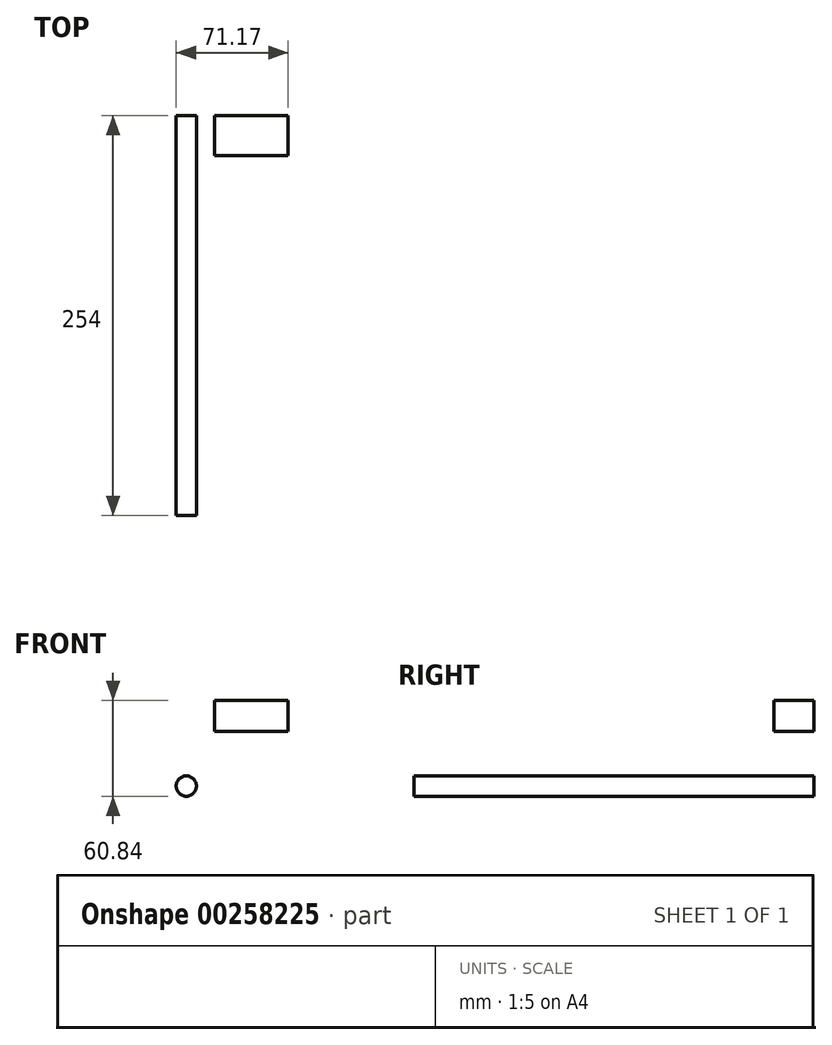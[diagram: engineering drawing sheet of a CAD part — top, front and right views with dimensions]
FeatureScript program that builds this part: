
annotation { "Feature Type Name" : "Feature", "Feature Type Description" : "" }
export const myFeature = defineFeature(function(context is Context, id is Id, definition is map)
    precondition{}
    {
        {
            var Q0;
            Q0=qCreatedBy(makeId("Front.planeOp"),FACE);
            var sketch = newSketch(context, id + "F0", { "sketchPlane" : qUnion([Q0])});
            skCircle(sketch, "E0", {"center": v(0, 0) * mm, "radius": 6.46 * mm});
            skLineSegment(sketch, "E1.bottom", {"start": v(17.88, 54.38) * mm, "end": v(64.7, 54.38) * mm});
            skLineSegment(sketch, "E1.top", {"start": v(17.88, 34.84) * mm, "end": v(64.7, 34.84) * mm});
            skLineSegment(sketch, "E1.left", {"start": v(17.88, 54.38) * mm, "end": v(17.88, 34.84) * mm});
            skLineSegment(sketch, "E1.right", {"start": v(64.7, 54.38) * mm, "end": v(64.7, 34.84) * mm});
            skSolve(sketch);
        }
        {
            var Q0;
            Q0=makeQuery(id+"F0.imprint","IMPRINT",FACE,{"disambiguationData":[TD([[makeQuery(id+"F0.imprint","IMPRINT",EDGE,{"derivedFrom":sQuery(id+"F0.wireOp",EDGE,"E0")}),1.0]])]});
            extrude(context, id + "F1", {"entities" : qUnion([Q0]), "depth" : 254 * mm});
        }
        {
            var Q0;
            Q0=makeQuery(id+"F0.imprint","IMPRINT",FACE,{"disambiguationData":[TD([[makeQuery(id+"F0.imprint","IMPRINT",EDGE,{"derivedFrom":sQuery(id+"F0.wireOp",EDGE,"E1.bottom")}),-1.0]])]});
            extrude(context, id + "F2", {"entities" : qUnion([Q0]), "depth" : 25.4 * mm});
        }
    });
